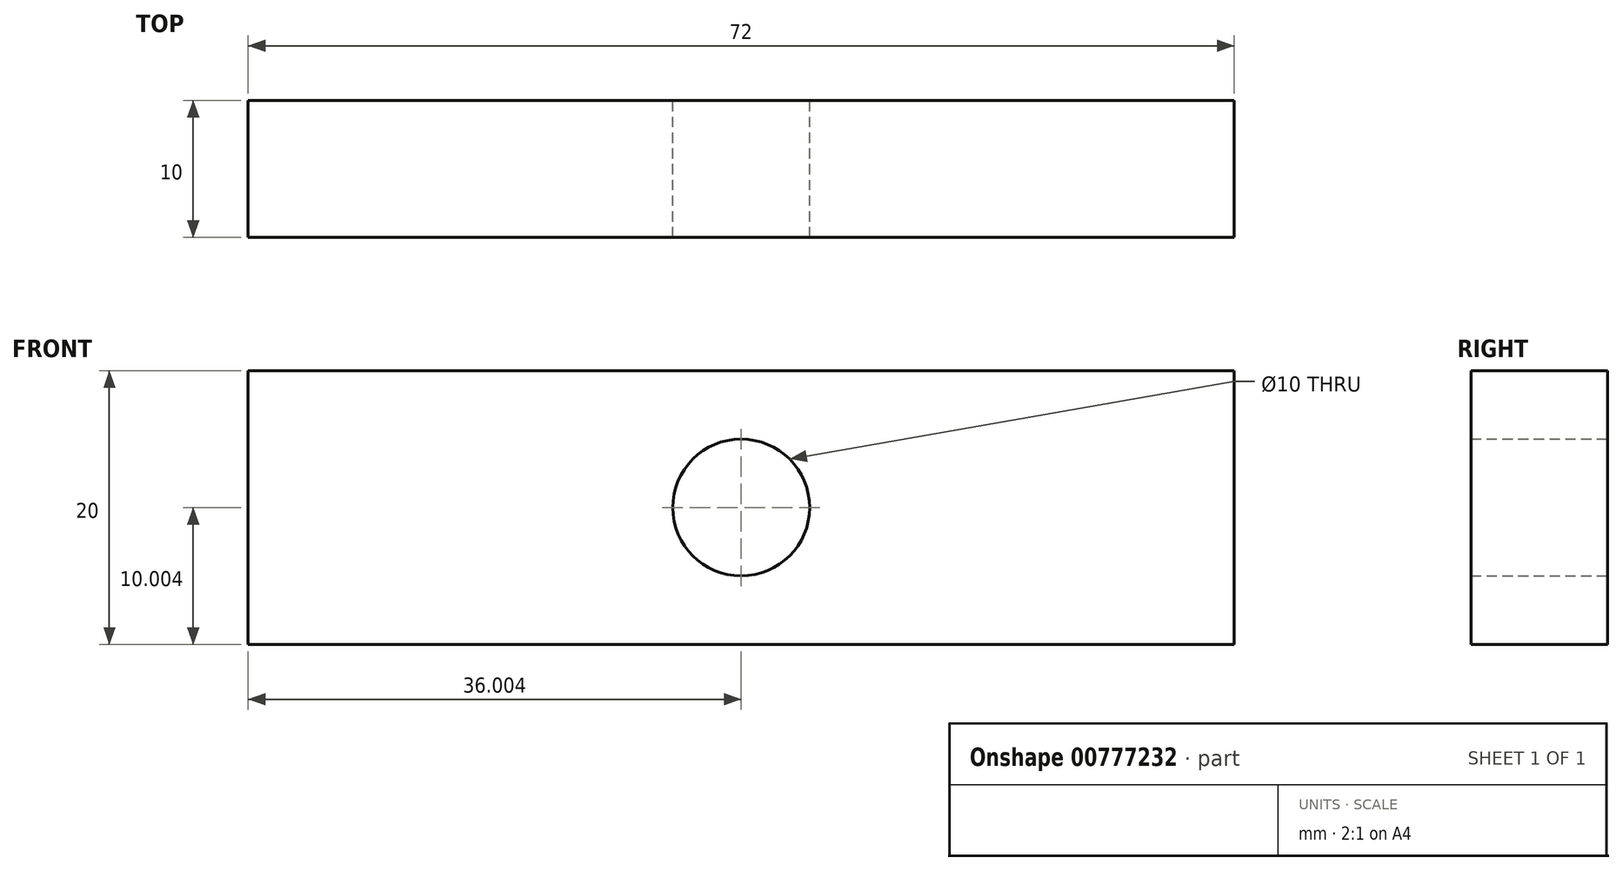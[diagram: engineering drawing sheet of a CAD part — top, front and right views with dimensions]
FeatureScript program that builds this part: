
annotation { "Feature Type Name" : "Feature", "Feature Type Description" : "" }
export const myFeature = defineFeature(function(context is Context, id is Id, definition is map)
    precondition{}
    {
        {
            var Q0;
            Q0=qCreatedBy(makeId("Front.planeOp"),FACE);
            var sketch = newSketch(context, id + "F0", { "sketchPlane" : qUnion([Q0])});
            skLineSegment(sketch, "E0.bottom", {"start": v(-42.97, 3.48) * mm, "end": v(29.03, 3.48) * mm});
            skLineSegment(sketch, "E0.top", {"start": v(-42.97, -16.52) * mm, "end": v(29.03, -16.52) * mm});
            skLineSegment(sketch, "E0.left", {"start": v(-42.97, 3.48) * mm, "end": v(-42.97, -16.52) * mm});
            skLineSegment(sketch, "E0.right", {"start": v(29.03, 3.48) * mm, "end": v(29.03, -16.52) * mm});
            skCircle(sketch, "E1", {"center": v(-6.97, -6.52) * mm, "radius": 5 * mm});
            skPoint(sketch, "E1.centerSnap0", {"position": v(-42.97, -6.52) * mm});
            skPoint(sketch, "E1.centerSnap1", {"position": v(-6.97, -16.52) * mm});
            skSolve(sketch);
        }
        {
            var Q0;
            Q0 = qSketchRegion(id + "F0", true);
            var Q1;
            Q1=makeQuery(id+"F0.imprint","IMPRINT",FACE,{"disambiguationData":[TD([[makeQuery(id+"F0.imprint","IMPRINT",EDGE,{"derivedFrom":sQuery(id+"F0.wireOp",EDGE,"E0.bottom")}),-1.0]])]});
            extrude(context, id + "F1", {"entities" : qUnion([Q0, Q1]), "depth" : 10 * mm, "offsetDistance" : 25 * mm});
        }
    });
